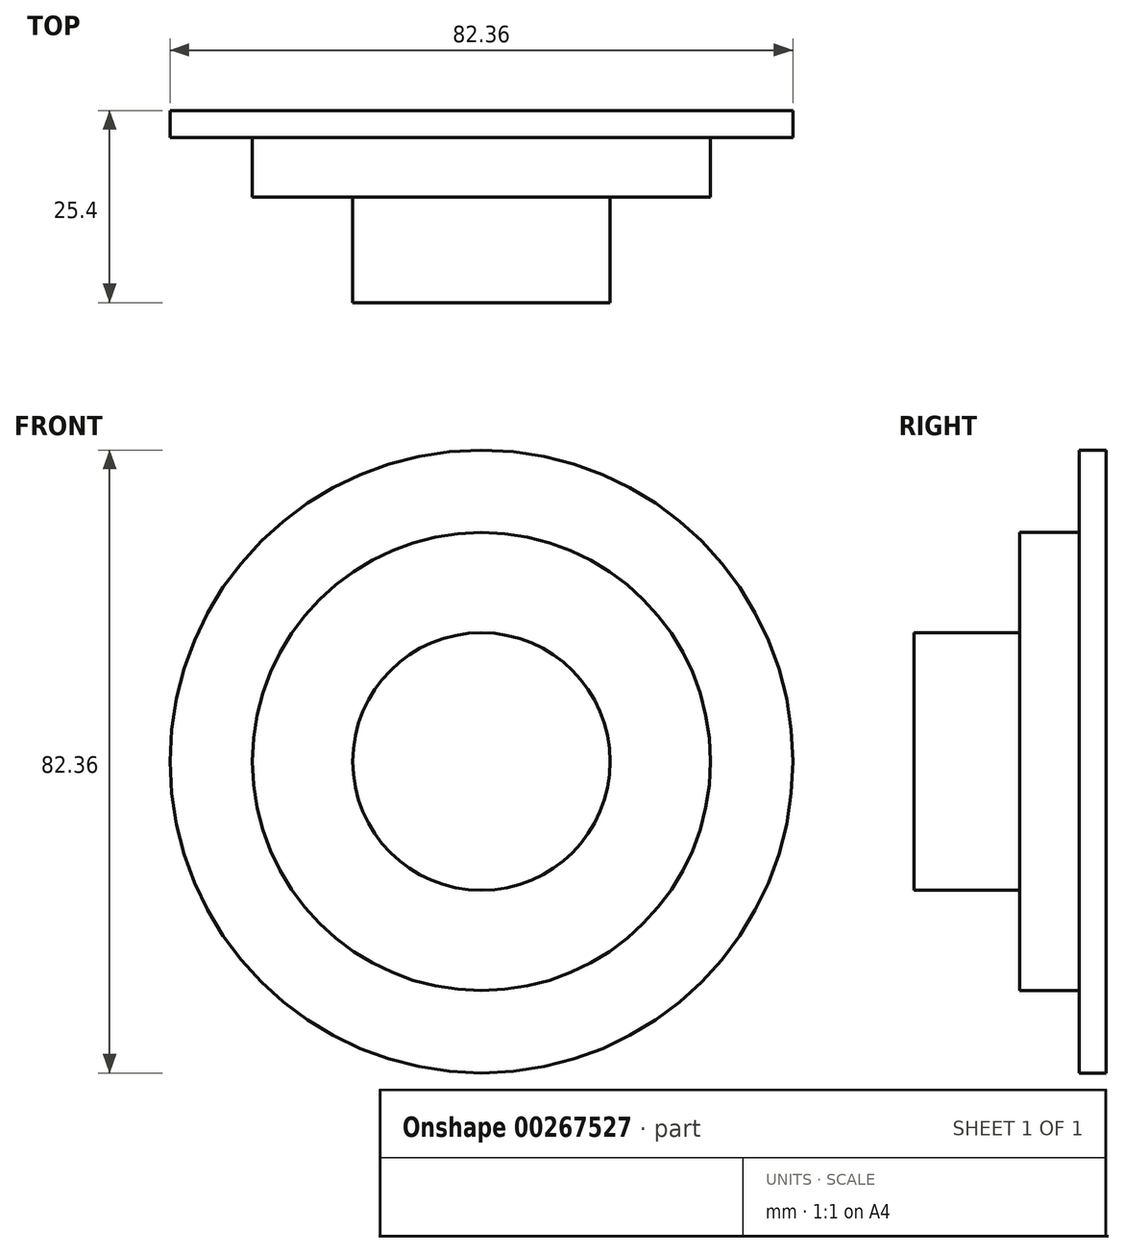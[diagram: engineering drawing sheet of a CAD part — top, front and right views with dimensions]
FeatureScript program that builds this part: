
annotation { "Feature Type Name" : "Feature", "Feature Type Description" : "" }
export const myFeature = defineFeature(function(context is Context, id is Id, definition is map)
    precondition{}
    {
        {
            var Q0;
            Q0=qCreatedBy(makeId("Front.planeOp"),FACE);
            var sketch = newSketch(context, id + "F0", { "sketchPlane" : qUnion([Q0])});
            skCircle(sketch, "E0", {"center": v(0, 0) * mm, "radius": 41.18 * mm});
            skSolve(sketch);
        }
        {
            var Q0;
            Q0=qCreatedBy(makeId("Front.planeOp"),FACE);
            var sketch = newSketch(context, id + "F1", { "sketchPlane" : qUnion([Q0])});
            skCircle(sketch, "E1", {"center": v(0, 0) * mm, "radius": 30.28 * mm});
            skSolve(sketch);
        }
        {
            var Q0;
            Q0=qCreatedBy(makeId("Front.planeOp"),FACE);
            var sketch = newSketch(context, id + "F2", { "sketchPlane" : qUnion([Q0])});
            skCircle(sketch, "E2", {"center": v(0, 0) * mm, "radius": 17.02 * mm});
            skSolve(sketch);
        }
        {
            var Q0;
            Q0 = qSketchRegion(id + "F2", true);
            extrude(context, id + "F3", {"entities" : qUnion([Q0]), "depth" : 25.4 * mm});
        }
        {
            var Q0;
            Q0=makeQuery(id+"F1.imprint","IMPRINT",FACE,{"disambiguationData":[TD([[makeQuery(id+"F1.imprint","IMPRINT",EDGE,{"derivedFrom":sQuery(id+"F1.wireOp",EDGE,"E1")}),1.0]])]});
            extrude(context, id + "F4", {"entities" : qUnion([Q0]), "operationType" : NewBodyOperationType.ADD, "depth" : 11.43 * mm});
        }
        {
            var Q0;
            Q0=makeQuery(id+"F0.imprint","IMPRINT",FACE,{"disambiguationData":[TD([[makeQuery(id+"F0.imprint","IMPRINT",EDGE,{"derivedFrom":sQuery(id+"F0.wireOp",EDGE,"E0")}),1.0]])]});
            extrude(context, id + "F5", {"entities" : qUnion([Q0]), "operationType" : NewBodyOperationType.ADD, "depth" : 3.56 * mm});
        }
    });
